# Revit family: QF_ELECTROLUXPROFESSIONAL_586637_PBEN30SCCM
name_source: partatom
category: Specialty Equipment
revit_build: Autodesk Revit 2018 (Build: 20190510_1515(x64)
units: mm (PartAtom-declared; Revit-internal decimal feet)

## family parameters
Always vertical = Yes
Cut with Voids When Loaded = No
Part Type = Normal
Room Calculation Point = No
Round Connector Dimension = Use Diameter
Shared = Yes
Work Plane-Based = No

## types (2) — shared parameters
Accessory = Yes
Compressed Air Pressure = 0.00 psi
Compressed Air Size = 0"
Compressed Air Volume = 0 GPM
Depth Actual = 900 mm  [stored 2.95276 ft]
Direct Waste Size = 0"
Gas Input Pressure = 0.0
Gas Size = 0"
HP = 0.4 HP
Height Actual = 700 mm  [stored 2.29659 ft]
Length Actual = 1400 mm  [stored 4.59318 ft]
Refrigerant Compressor Remote = Yes
Refrigeration Liquid Line Size = 0"
Refrigeration Suction Line Size = 0"
Steam Consumption per Hour = 130
Steam Supply Maximum Pressure = 0.00 psi
Steam Supply Minimum Pressure = 0.00 psi
Watts = 0 W
Weight = 0.00 kg
zero-valued in all types: Gas KW

## per-type parameters (varying)
| type | Cold Water Size | Condensate Return Size | Cycle | Description | Hot Water Size | Item Number | Manufacturer | Model | Phase | Steam Supply Size | URL | URL Manufacturer | Volts |
| 586637 | 0" | 0" | 0 Hz | High Productivity Cooking Steam Rectangular Boiling Pan-80lt Hygienic Profile-Freestanding | 0" |  | ELECTROLUX | 586637 | 0 | 0" | www.electrolux.com/foodservice |  | 0 V |
| QF_ELECTROLUX_586637_PBEN30SCCM | 1" | 1" | 60 Hz | STEAM BOILING P+TAP,RECT,300L(H),FS,D900 | 1" | 586637 | Electrolux | PBEN30SCCM | 1 | 1" | http://professional.electrolux.com | http://professional.electrolux.com | 230 V |

note: source unit labels omitted for Gas Input Pressure — the stored unit's dimension contradicts the parameter name (converter mislabeling)

note: [stored X ft] marks values corroborated as IEEE doubles in the binary element streams (Revit-internal decimal feet)

## geometry (parser evidence)
native form markers: Blend x33, Sweep x6
no freeform markers — native parametric forms only
